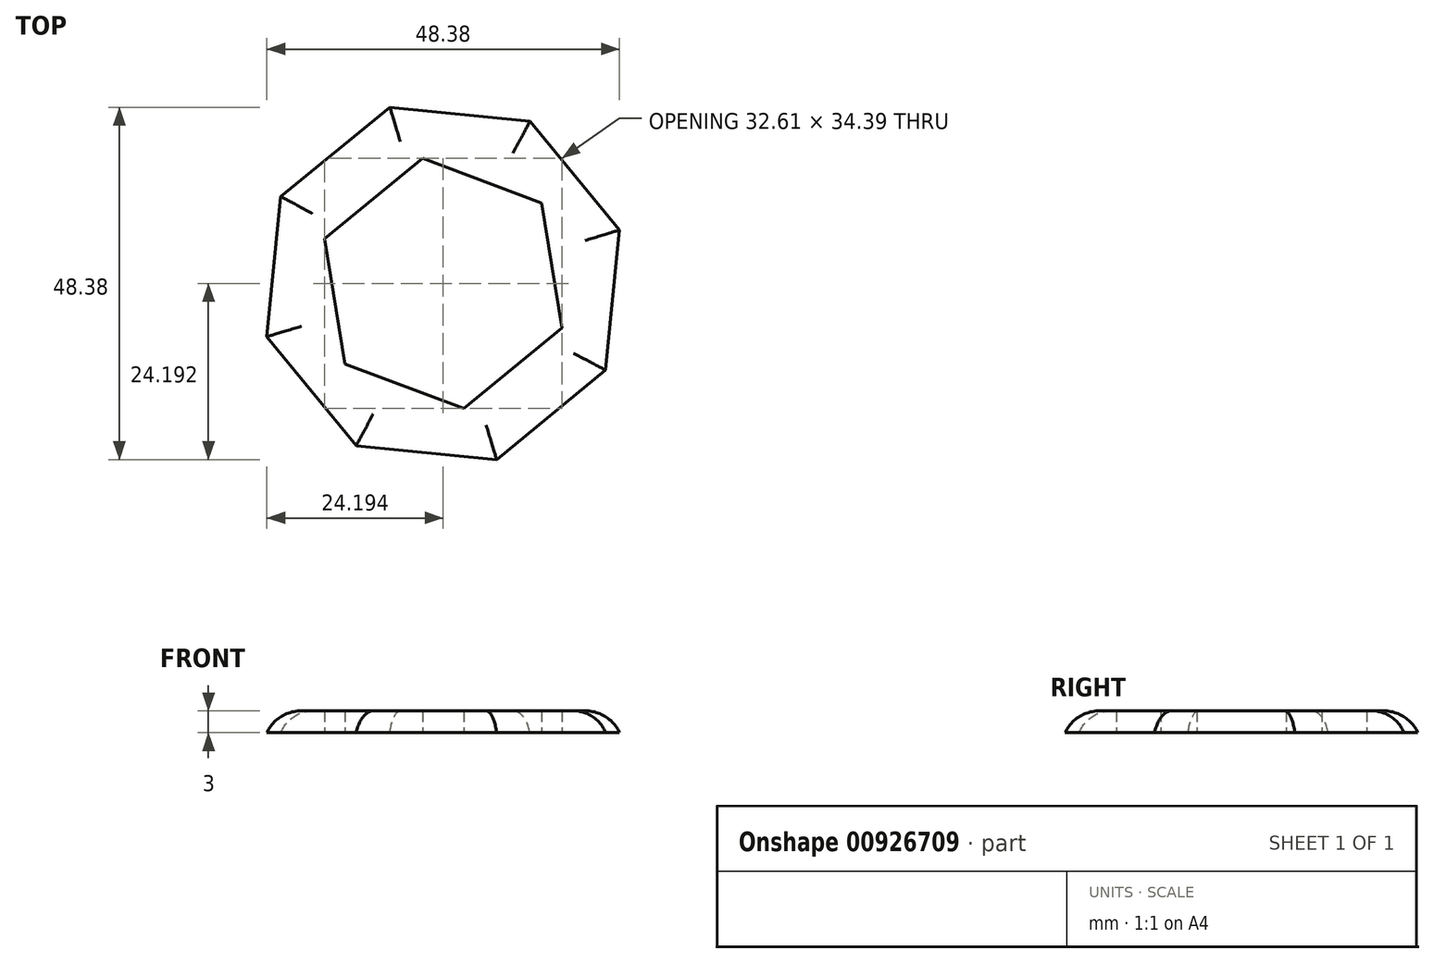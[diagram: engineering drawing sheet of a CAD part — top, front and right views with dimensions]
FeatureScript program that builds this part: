
annotation { "Feature Type Name" : "Feature", "Feature Type Description" : "" }
export const myFeature = defineFeature(function(context is Context, id is Id, definition is map)
    precondition{}
    {
        {
            var Q0;
            Q0=qCreatedBy(makeId("Top.planeOp"),FACE);
            var sketch = newSketch(context, id + "F0", { "sketchPlane" : qUnion([Q0])});
            skCircle(sketch, "E0.cCircle", {"center": v(-64.02, 18.12) * mm, "radius": 23.35 * mm, "construction": true});
            skLineSegment(sketch, "E0.0", {"start": v(-41.73, 6.2) * mm, "end": v(-56.7, -6.07) * mm});
            skLineSegment(sketch, "E0.1", {"start": v(-56.7, -6.07) * mm, "end": v(-75.94, -4.16) * mm});
            skLineSegment(sketch, "E0.2", {"start": v(-75.94, -4.16) * mm, "end": v(-88.2, 10.8) * mm});
            skLineSegment(sketch, "E0.3", {"start": v(-88.2, 10.8) * mm, "end": v(-86.3, 30.05) * mm});
            skLineSegment(sketch, "E0.4", {"start": v(-86.3, 30.05) * mm, "end": v(-71.34, 42.31) * mm});
            skLineSegment(sketch, "E0.5", {"start": v(-71.34, 42.31) * mm, "end": v(-52.09, 40.4) * mm});
            skLineSegment(sketch, "E0.6", {"start": v(-52.09, 40.4) * mm, "end": v(-39.83, 25.44) * mm});
            skLineSegment(sketch, "E0.7", {"start": v(-39.83, 25.44) * mm, "end": v(-41.73, 6.2) * mm});
            skPoint(sketch, "E0.0.midPoint", {"position": v(-49.21, 0.06) * mm});
            skCircle(sketch, "E1.cCircle", {"center": v(-64.02, 18.12) * mm, "radius": 15.1 * mm, "construction": true});
            skLineSegment(sketch, "E1.0", {"start": v(-80.32, 24.27) * mm, "end": v(-66.84, 35.32) * mm});
            skLineSegment(sketch, "E1.1", {"start": v(-66.84, 35.32) * mm, "end": v(-50.54, 29.17) * mm});
            skLineSegment(sketch, "E1.2", {"start": v(-50.54, 29.17) * mm, "end": v(-47.7, 11.97) * mm});
            skLineSegment(sketch, "E1.3", {"start": v(-47.7, 11.97) * mm, "end": v(-61.19, 0.92) * mm});
            skLineSegment(sketch, "E1.4", {"start": v(-61.19, 0.92) * mm, "end": v(-77.5, 7.07) * mm});
            skLineSegment(sketch, "E1.5", {"start": v(-77.5, 7.07) * mm, "end": v(-80.32, 24.27) * mm});
            skPoint(sketch, "E1.0.midPoint", {"position": v(-73.58, 29.8) * mm});
            skSolve(sketch);
        }
        {
            var Q0;
            Q0=makeQuery(id+"F0.imprint","IMPRINT",FACE,{"disambiguationData":[TD([[makeQuery(id+"F0.imprint","IMPRINT",EDGE,{"derivedFrom":sQuery(id+"F0.wireOp",EDGE,"E0.0")}),-1.0]])]});
            extrude(context, id + "F1", {"entities" : qUnion([Q0]), "depth" : 3 * mm, "offsetDistance" : 25 * mm});
        }
        {
            var Q0;
            Q0=makeQuery(id+"F1.opExtrude","CAP_EDGE",EDGE,{"disambiguationData":[OSD([sQuery(id+"F0.wireOp",EDGE,"E0.5")])],"isStart":false});
            var Q1;
            Q1=makeQuery(id+"F1.opExtrude","CAP_EDGE",EDGE,{"disambiguationData":[OSD([sQuery(id+"F0.wireOp",EDGE,"E0.4")])],"isStart":false});
            var Q2;
            Q2=makeQuery(id+"F1.opExtrude","CAP_EDGE",EDGE,{"disambiguationData":[OSD([sQuery(id+"F0.wireOp",EDGE,"E0.3")])],"isStart":false});
            var Q3;
            Q3=makeQuery(id+"F1.opExtrude","CAP_EDGE",EDGE,{"disambiguationData":[OSD([sQuery(id+"F0.wireOp",EDGE,"E0.2")])],"isStart":false});
            var Q4;
            Q4=makeQuery(id+"F1.opExtrude","CAP_EDGE",EDGE,{"disambiguationData":[OSD([sQuery(id+"F0.wireOp",EDGE,"E0.1")])],"isStart":false});
            var Q5;
            Q5=makeQuery(id+"F1.opExtrude","CAP_EDGE",EDGE,{"disambiguationData":[OSD([sQuery(id+"F0.wireOp",EDGE,"E0.0")])],"isStart":false});
            var Q6;
            Q6=makeQuery(id+"F1.opExtrude","CAP_EDGE",EDGE,{"disambiguationData":[OSD([sQuery(id+"F0.wireOp",EDGE,"E0.7")])],"isStart":false});
            var Q7;
            Q7=makeQuery(id+"F1.opExtrude","CAP_EDGE",EDGE,{"disambiguationData":[OSD([sQuery(id+"F0.wireOp",EDGE,"E0.6")])],"isStart":false});
            fillet(context, id + "F2", {"entities" : qUnion([Q0, Q1, Q2, Q3, Q4, Q5, Q6, Q7]), "radius" : 5 * mm, "tangentPropagation" : true, "allowEdgeOverflow" : false});
        }
    });
